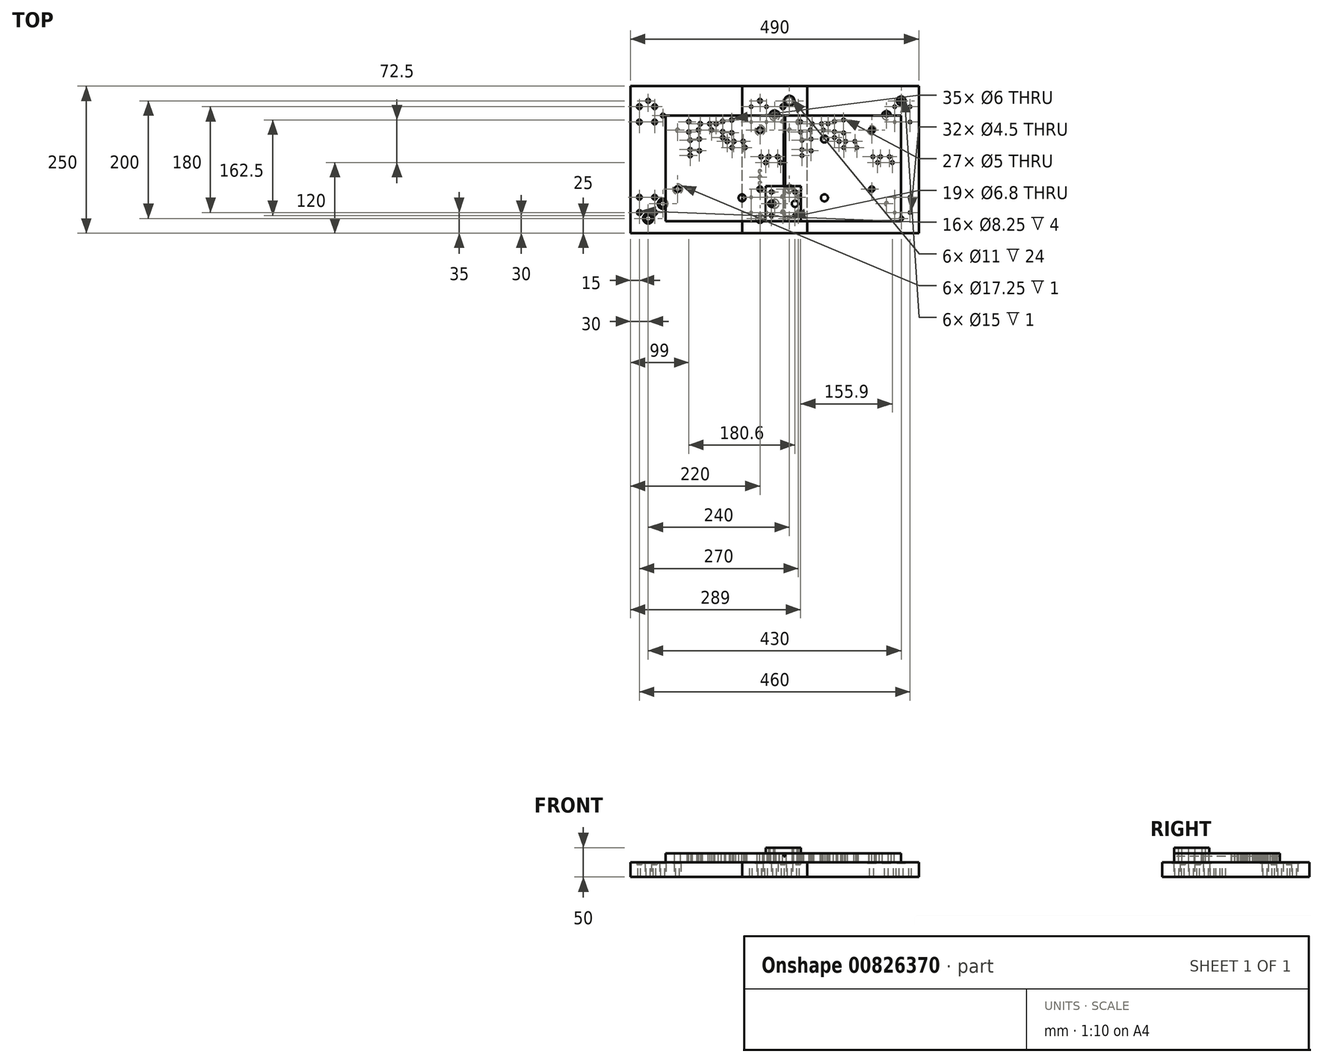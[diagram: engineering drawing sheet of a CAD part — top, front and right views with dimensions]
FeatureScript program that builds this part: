
annotation { "Feature Type Name" : "Feature", "Feature Type Description" : "" }
export const myFeature = defineFeature(function(context is Context, id is Id, definition is map)
    precondition{}
    {
        {
            var Q0;
            Q0=qCreatedBy(makeId("Top.planeOp"),FACE);
            var sketch = newSketch(context, id + "F0", { "sketchPlane" : qUnion([Q0])});
            skLineSegment(sketch, "E0.bottom", {"start": v(0, 0) * mm, "end": v(190, 0) * mm});
            skLineSegment(sketch, "E0.top", {"start": v(0, -180) * mm, "end": v(190, -180) * mm});
            skLineSegment(sketch, "E0.left", {"start": v(0, 0) * mm, "end": v(0, -180) * mm});
            skLineSegment(sketch, "E0.right", {"start": v(190, 0) * mm, "end": v(190, -180) * mm});
            skLineSegment(sketch, "E1", {"start": v(39.4, -10.5) * mm, "end": v(39.4, -28) * mm});
            skLineSegment(sketch, "E2", {"start": v(41.8, -42) * mm, "end": v(41.8, -58) * mm});
            skCircle(sketch, "E3", {"center": v(39.4, -10.5) * mm, "radius": 3 * mm});
            skCircle(sketch, "E4", {"center": v(39.4, -28) * mm, "radius": 3 * mm});
            skLineSegment(sketch, "E5", {"start": v(41.8, -58) * mm, "end": v(41.8, -68) * mm});
            skCircle(sketch, "E6", {"center": v(41.8, -42) * mm, "radius": 3 * mm});
            skCircle(sketch, "E7", {"center": v(41.8, -58) * mm, "radius": 3 * mm});
            skCircle(sketch, "E8", {"center": v(41.8, -68) * mm, "radius": 3 * mm});
            skLineSegment(sketch, "E9", {"start": v(59, -14) * mm, "end": v(75, -14) * mm});
            skLineSegment(sketch, "E10", {"start": v(75, -14) * mm, "end": v(86, -14) * mm});
            skLineSegment(sketch, "E11", {"start": v(56, -24.5) * mm, "end": v(78, -24.5) * mm});
            skCircle(sketch, "E12", {"center": v(59, -14) * mm, "radius": 3 * mm});
            skCircle(sketch, "E13", {"center": v(56, -24.5) * mm, "radius": 3 * mm});
            skCircle(sketch, "E14", {"center": v(78, -24.5) * mm, "radius": 3 * mm});
            skCircle(sketch, "E15", {"center": v(86, -14) * mm, "radius": 3 * mm});
            skCircle(sketch, "E16", {"center": v(75, -14) * mm, "radius": 3 * mm});
            skLineSegment(sketch, "E17", {"start": v(57.3, -40) * mm, "end": v(57.3, -60) * mm});
            skCircle(sketch, "E18", {"center": v(57.3, -40) * mm, "radius": 3 * mm});
            skCircle(sketch, "E19", {"center": v(57.3, -60) * mm, "radius": 3 * mm});
            skLineSegment(sketch, "E20", {"start": v(97, -10) * mm, "end": v(97, -27.5) * mm});
            skLineSegment(sketch, "E21", {"start": v(97, -27.5) * mm, "end": v(97, -37.5) * mm});
            skCircle(sketch, "E22", {"center": v(97, -10) * mm, "radius": 3 * mm});
            skCircle(sketch, "E23", {"center": v(97, -27.5) * mm, "radius": 3 * mm});
            skCircle(sketch, "E24", {"center": v(97, -37.5) * mm, "radius": 3 * mm});
            skLineSegment(sketch, "E25", {"start": v(104.9, -44) * mm, "end": v(112.9, -54.5) * mm});
            skLineSegment(sketch, "E26", {"start": v(112.9, -54.5) * mm, "end": v(134.9, -54.5) * mm});
            skCircle(sketch, "E27", {"center": v(104.9, -44) * mm, "radius": 3 * mm});
            skCircle(sketch, "E28", {"center": v(112.9, -54.5) * mm, "radius": 3 * mm});
            skCircle(sketch, "E29", {"center": v(134.9, -54.5) * mm, "radius": 3 * mm});
            skLineSegment(sketch, "E30", {"start": v(112.5, -7.5) * mm, "end": v(112.5, -29.5) * mm});
            skCircle(sketch, "E31", {"center": v(112.5, -7.5) * mm, "radius": 3 * mm});
            skCircle(sketch, "E32", {"center": v(112.5, -29.5) * mm, "radius": 3 * mm});
            skLineSegment(sketch, "E33", {"start": v(115.9, -44) * mm, "end": v(131.9, -44) * mm});
            skCircle(sketch, "E34", {"center": v(115.9, -44) * mm, "radius": 3 * mm});
            skCircle(sketch, "E35", {"center": v(131.9, -44) * mm, "radius": 3 * mm});
            skLineSegment(sketch, "E36.bottom", {"start": v(190, 0) * mm, "end": v(400, 0) * mm});
            skLineSegment(sketch, "E36.top", {"start": v(190, -180) * mm, "end": v(400, -180) * mm});
            skLineSegment(sketch, "E36.right", {"start": v(400, 0) * mm, "end": v(400, -180) * mm});
            skLineSegment(sketch, "E37", {"start": v(229.4, -10.5) * mm, "end": v(229.4, -28) * mm});
            skLineSegment(sketch, "E38", {"start": v(231.8, -42) * mm, "end": v(231.8, -58) * mm});
            skCircle(sketch, "E39", {"center": v(229.4, -10.5) * mm, "radius": 2.5 * mm});
            skCircle(sketch, "E40", {"center": v(229.4, -28) * mm, "radius": 2.5 * mm});
            skLineSegment(sketch, "E41", {"start": v(231.8, -58) * mm, "end": v(231.8, -68) * mm});
            skCircle(sketch, "E42", {"center": v(231.8, -42) * mm, "radius": 2.5 * mm});
            skCircle(sketch, "E43", {"center": v(231.8, -58) * mm, "radius": 2.5 * mm});
            skCircle(sketch, "E44", {"center": v(231.8, -68) * mm, "radius": 2.5 * mm});
            skLineSegment(sketch, "E45", {"start": v(249, -14) * mm, "end": v(265, -14) * mm});
            skLineSegment(sketch, "E46", {"start": v(265, -14) * mm, "end": v(276, -14) * mm});
            skLineSegment(sketch, "E47", {"start": v(246, -24.5) * mm, "end": v(268, -24.5) * mm});
            skCircle(sketch, "E48", {"center": v(249, -14) * mm, "radius": 2.5 * mm});
            skCircle(sketch, "E49", {"center": v(246, -24.5) * mm, "radius": 2.5 * mm});
            skCircle(sketch, "E50", {"center": v(268, -24.5) * mm, "radius": 2.5 * mm});
            skCircle(sketch, "E51", {"center": v(276, -14) * mm, "radius": 2.5 * mm});
            skCircle(sketch, "E52", {"center": v(265, -14) * mm, "radius": 2.5 * mm});
            skLineSegment(sketch, "E53", {"start": v(247.3, -40) * mm, "end": v(247.3, -60) * mm});
            skCircle(sketch, "E54", {"center": v(247.3, -40) * mm, "radius": 2.5 * mm});
            skCircle(sketch, "E55", {"center": v(247.3, -60) * mm, "radius": 2.5 * mm});
            skLineSegment(sketch, "E56", {"start": v(287, -10) * mm, "end": v(287, -27.5) * mm});
            skLineSegment(sketch, "E57", {"start": v(287, -27.5) * mm, "end": v(287, -37.5) * mm});
            skCircle(sketch, "E58", {"center": v(287, -10) * mm, "radius": 2.5 * mm});
            skCircle(sketch, "E59", {"center": v(287, -27.5) * mm, "radius": 2.5 * mm});
            skCircle(sketch, "E60", {"center": v(287, -37.5) * mm, "radius": 2.5 * mm});
            skLineSegment(sketch, "E61", {"start": v(294.9, -44) * mm, "end": v(302.9, -54.5) * mm});
            skLineSegment(sketch, "E62", {"start": v(302.9, -54.5) * mm, "end": v(324.9, -54.5) * mm});
            skCircle(sketch, "E63", {"center": v(294.9, -44) * mm, "radius": 2.5 * mm});
            skCircle(sketch, "E64", {"center": v(302.9, -54.5) * mm, "radius": 2.5 * mm});
            skCircle(sketch, "E65", {"center": v(324.9, -54.5) * mm, "radius": 2.5 * mm});
            skLineSegment(sketch, "E66", {"start": v(302.5, -7.5) * mm, "end": v(302.5, -29.5) * mm});
            skCircle(sketch, "E67", {"center": v(302.5, -7.5) * mm, "radius": 2.5 * mm});
            skCircle(sketch, "E68", {"center": v(302.5, -29.5) * mm, "radius": 2.5 * mm});
            skLineSegment(sketch, "E69", {"start": v(305.9, -44) * mm, "end": v(321.9, -44) * mm});
            skCircle(sketch, "E70", {"center": v(305.9, -44) * mm, "radius": 2.5 * mm});
            skCircle(sketch, "E71", {"center": v(321.9, -44) * mm, "radius": 2.5 * mm});
            skCircle(sketch, "E72", {"center": v(162.3, -70) * mm, "radius": 3 * mm});
            skCircle(sketch, "E73", {"center": v(175.3, -70) * mm, "radius": 3 * mm});
            skCircle(sketch, "E74", {"center": v(190.3, -70) * mm, "radius": 3 * mm});
            skCircle(sketch, "E75", {"center": v(170.3, -80) * mm, "radius": 3 * mm});
            skCircle(sketch, "E76", {"center": v(195.3, -80) * mm, "radius": 3 * mm});
            skLineSegment(sketch, "E77", {"start": v(162.3, -70) * mm, "end": v(175.3, -70) * mm});
            skLineSegment(sketch, "E78", {"start": v(175.3, -70) * mm, "end": v(190.3, -70) * mm});
            skLineSegment(sketch, "E79", {"start": v(170.3, -80) * mm, "end": v(195.3, -80) * mm});
            skCircle(sketch, "E80", {"center": v(352.3, -70) * mm, "radius": 2.5 * mm});
            skCircle(sketch, "E81", {"center": v(380.3, -70) * mm, "radius": 2.5 * mm});
            skCircle(sketch, "E82", {"center": v(365.3, -70) * mm, "radius": 2.5 * mm});
            skCircle(sketch, "E83", {"center": v(360.3, -80) * mm, "radius": 2.5 * mm});
            skCircle(sketch, "E84", {"center": v(385.3, -80) * mm, "radius": 2.5 * mm});
            skLineSegment(sketch, "E85", {"start": v(352.3, -70) * mm, "end": v(380.3, -70) * mm});
            skLineSegment(sketch, "E86", {"start": v(365.3, -70) * mm, "end": v(380.3, -70) * mm});
            skLineSegment(sketch, "E87", {"start": v(360.3, -80) * mm, "end": v(385.3, -80) * mm});
            skCircle(sketch, "E88", {"center": v(130, -140) * mm, "radius": 6 * mm});
            skCircle(sketch, "E89", {"center": v(270, -140) * mm, "radius": 6 * mm});
            skCircle(sketch, "E90", {"center": v(270, -40) * mm, "radius": 6 * mm});
            skLineSegment(sketch, "E91", {"start": v(200, -180) * mm, "end": v(200, 0) * mm});
            skSolve(sketch);
        }
        {
            var Q0;
            Q0 = qSketchRegion(id + "F0", true);
            extrude(context, id + "F1", {"entities" : qUnion([Q0]), "depth" : 15 * mm, "offsetDistance" : 25 * mm});
        }
        {
            var Q0;
            Q0=makeQuery(id+"F1.opExtrude","CAP_FACE",FACE,{"disambiguationData":[OSD([sQuery(id+"F0.wireOp",EDGE,"E0.bottom"),sQuery(id+"F0.wireOp",EDGE,"E0.top"),sQuery(id+"F0.wireOp",EDGE,"E0.left"),sQuery(id+"F0.wireOp",EDGE,"E3"),sQuery(id+"F0.wireOp",EDGE,"E4"),sQuery(id+"F0.wireOp",EDGE,"E6"),sQuery(id+"F0.wireOp",EDGE,"E7"),sQuery(id+"F0.wireOp",EDGE,"E8"),sQuery(id+"F0.wireOp",EDGE,"E12"),sQuery(id+"F0.wireOp",EDGE,"E13"),sQuery(id+"F0.wireOp",EDGE,"E14"),sQuery(id+"F0.wireOp",EDGE,"E15"),sQuery(id+"F0.wireOp",EDGE,"E16"),sQuery(id+"F0.wireOp",EDGE,"E18"),sQuery(id+"F0.wireOp",EDGE,"E19"),sQuery(id+"F0.wireOp",EDGE,"E22"),sQuery(id+"F0.wireOp",EDGE,"E23"),sQuery(id+"F0.wireOp",EDGE,"E24"),sQuery(id+"F0.wireOp",EDGE,"E27"),sQuery(id+"F0.wireOp",EDGE,"E28"),sQuery(id+"F0.wireOp",EDGE,"E29"),sQuery(id+"F0.wireOp",EDGE,"E31"),sQuery(id+"F0.wireOp",EDGE,"E32"),sQuery(id+"F0.wireOp",EDGE,"E34"),sQuery(id+"F0.wireOp",EDGE,"E35"),sQuery(id+"F0.wireOp",EDGE,"E36.bottom"),sQuery(id+"F0.wireOp",EDGE,"E36.top"),sQuery(id+"F0.wireOp",EDGE,"E36.right"),sQuery(id+"F0.wireOp",EDGE,"E39"),sQuery(id+"F0.wireOp",EDGE,"E40"),sQuery(id+"F0.wireOp",EDGE,"E42"),sQuery(id+"F0.wireOp",EDGE,"E43"),sQuery(id+"F0.wireOp",EDGE,"E44"),sQuery(id+"F0.wireOp",EDGE,"E48"),sQuery(id+"F0.wireOp",EDGE,"E49"),sQuery(id+"F0.wireOp",EDGE,"E50"),sQuery(id+"F0.wireOp",EDGE,"E51"),sQuery(id+"F0.wireOp",EDGE,"E52"),sQuery(id+"F0.wireOp",EDGE,"E54"),sQuery(id+"F0.wireOp",EDGE,"E55"),sQuery(id+"F0.wireOp",EDGE,"E58"),sQuery(id+"F0.wireOp",EDGE,"E59"),sQuery(id+"F0.wireOp",EDGE,"E60"),sQuery(id+"F0.wireOp",EDGE,"E63"),sQuery(id+"F0.wireOp",EDGE,"E64"),sQuery(id+"F0.wireOp",EDGE,"E65"),sQuery(id+"F0.wireOp",EDGE,"E67"),sQuery(id+"F0.wireOp",EDGE,"E68"),sQuery(id+"F0.wireOp",EDGE,"E70"),sQuery(id+"F0.wireOp",EDGE,"E71"),sQuery(id+"F0.wireOp",EDGE,"E72"),sQuery(id+"F0.wireOp",EDGE,"E73"),sQuery(id+"F0.wireOp",EDGE,"E74"),sQuery(id+"F0.wireOp",EDGE,"E75"),sQuery(id+"F0.wireOp",EDGE,"E76"),sQuery(id+"F0.wireOp",EDGE,"E80"),sQuery(id+"F0.wireOp",EDGE,"E81"),sQuery(id+"F0.wireOp",EDGE,"E82"),sQuery(id+"F0.wireOp",EDGE,"E83"),sQuery(id+"F0.wireOp",EDGE,"E84")])],"isStart":false});
            var sketch = newSketch(context, id + "F2", { "sketchPlane" : qUnion([Q0])});
            skLineSegment(sketch, "E92.bottom", {"start": v(170, -120) * mm, "end": v(230, -120) * mm});
            skLineSegment(sketch, "E92.top", {"start": v(170, -180) * mm, "end": v(230, -180) * mm});
            skLineSegment(sketch, "E92.left", {"start": v(170, -120) * mm, "end": v(170, -180) * mm});
            skLineSegment(sketch, "E92.right", {"start": v(230, -120) * mm, "end": v(230, -180) * mm});
            skCircle(sketch, "E93", {"center": v(180, -170) * mm, "radius": 2.5 * mm});
            skCircle(sketch, "E94", {"center": v(180, -150) * mm, "radius": 2.5 * mm});
            skCircle(sketch, "E95", {"center": v(180, -130) * mm, "radius": 2.5 * mm});
            skCircle(sketch, "E96", {"center": v(220, -130) * mm, "radius": 2.5 * mm});
            skCircle(sketch, "E97", {"center": v(220, -150) * mm, "radius": 2.5 * mm});
            skCircle(sketch, "E98", {"center": v(220, -170) * mm, "radius": 2.5 * mm});
            skPoint(sketch, "E99", {"position": v(200, -125.79) * mm});
            skPoint(sketch, "E100", {"position": v(170, -150) * mm});
            skPoint(sketch, "E101", {"position": v(200, -120) * mm});
            skSolve(sketch);
        }
        {
            var Q0;
            Q0 = qSketchRegion(id + "F2", true);
            extrude(context, id + "F3", {"entities" : qUnion([Q0]), "depth" : 10 * mm, "offsetDistance" : 25 * mm});
        }
        {
            var Q0;
            Q0=makeQuery(id+"F3.opExtrude","CAP_FACE",FACE,{"disambiguationData":[OSD([sQuery(id+"F2.wireOp",EDGE,"E92.bottom"),sQuery(id+"F2.wireOp",EDGE,"E92.top"),sQuery(id+"F2.wireOp",EDGE,"E92.left"),sQuery(id+"F2.wireOp",EDGE,"E92.right"),sQuery(id+"F2.wireOp",EDGE,"E93"),sQuery(id+"F2.wireOp",EDGE,"E94"),sQuery(id+"F2.wireOp",EDGE,"E95"),sQuery(id+"F2.wireOp",EDGE,"E96"),sQuery(id+"F2.wireOp",EDGE,"E97"),sQuery(id+"F2.wireOp",EDGE,"E98")])],"isStart":false});
            var sketch = newSketch(context, id + "F4", { "sketchPlane" : qUnion([Q0])});
            skPoint(sketch, "E102", {"position": v(180, -170) * mm});
            skPoint(sketch, "E103", {"position": v(180, -150) * mm});
            skPoint(sketch, "E104", {"position": v(180, -130) * mm});
            skPoint(sketch, "E105", {"position": v(220, -130) * mm});
            skPoint(sketch, "E106", {"position": v(220, -150) * mm});
            skPoint(sketch, "E107", {"position": v(220, -170) * mm});
            skSolve(sketch);
        }
        {
            var Q0;
            Q0=sQuery(id+"F4.wireOp",VERTEX,"E103");
            var Q1;
            Q1=sQuery(id+"F4.wireOp",VERTEX,"E106");
            var Q2;
            Q2=makeQuery(id+"F1.opExtrude","SWEPT_BODY",BODY,{"disambiguationData":[OSD([sQuery(id+"F0.wireOp",EDGE,"E0.bottom"),sQuery(id+"F0.wireOp",EDGE,"E0.top"),sQuery(id+"F0.wireOp",EDGE,"E0.left"),sQuery(id+"F0.wireOp",EDGE,"E3"),sQuery(id+"F0.wireOp",EDGE,"E4"),sQuery(id+"F0.wireOp",EDGE,"E6"),sQuery(id+"F0.wireOp",EDGE,"E7"),sQuery(id+"F0.wireOp",EDGE,"E8"),sQuery(id+"F0.wireOp",EDGE,"E12"),sQuery(id+"F0.wireOp",EDGE,"E13"),sQuery(id+"F0.wireOp",EDGE,"E14"),sQuery(id+"F0.wireOp",EDGE,"E15"),sQuery(id+"F0.wireOp",EDGE,"E16"),sQuery(id+"F0.wireOp",EDGE,"E18"),sQuery(id+"F0.wireOp",EDGE,"E19"),sQuery(id+"F0.wireOp",EDGE,"E22"),sQuery(id+"F0.wireOp",EDGE,"E23"),sQuery(id+"F0.wireOp",EDGE,"E24"),sQuery(id+"F0.wireOp",EDGE,"E27"),sQuery(id+"F0.wireOp",EDGE,"E28"),sQuery(id+"F0.wireOp",EDGE,"E29"),sQuery(id+"F0.wireOp",EDGE,"E31"),sQuery(id+"F0.wireOp",EDGE,"E32"),sQuery(id+"F0.wireOp",EDGE,"E34"),sQuery(id+"F0.wireOp",EDGE,"E35"),sQuery(id+"F0.wireOp",EDGE,"E36.bottom"),sQuery(id+"F0.wireOp",EDGE,"E36.top"),sQuery(id+"F0.wireOp",EDGE,"E36.right"),sQuery(id+"F0.wireOp",EDGE,"E39"),sQuery(id+"F0.wireOp",EDGE,"E40"),sQuery(id+"F0.wireOp",EDGE,"E42"),sQuery(id+"F0.wireOp",EDGE,"E43"),sQuery(id+"F0.wireOp",EDGE,"E44"),sQuery(id+"F0.wireOp",EDGE,"E48"),sQuery(id+"F0.wireOp",EDGE,"E49"),sQuery(id+"F0.wireOp",EDGE,"E50"),sQuery(id+"F0.wireOp",EDGE,"E51"),sQuery(id+"F0.wireOp",EDGE,"E52"),sQuery(id+"F0.wireOp",EDGE,"E54"),sQuery(id+"F0.wireOp",EDGE,"E55"),sQuery(id+"F0.wireOp",EDGE,"E58"),sQuery(id+"F0.wireOp",EDGE,"E59"),sQuery(id+"F0.wireOp",EDGE,"E60"),sQuery(id+"F0.wireOp",EDGE,"E63"),sQuery(id+"F0.wireOp",EDGE,"E64"),sQuery(id+"F0.wireOp",EDGE,"E65"),sQuery(id+"F0.wireOp",EDGE,"E67"),sQuery(id+"F0.wireOp",EDGE,"E68"),sQuery(id+"F0.wireOp",EDGE,"E70"),sQuery(id+"F0.wireOp",EDGE,"E71"),sQuery(id+"F0.wireOp",EDGE,"E72"),sQuery(id+"F0.wireOp",EDGE,"E73"),sQuery(id+"F0.wireOp",EDGE,"E74"),sQuery(id+"F0.wireOp",EDGE,"E75"),sQuery(id+"F0.wireOp",EDGE,"E76"),sQuery(id+"F0.wireOp",EDGE,"E80"),sQuery(id+"F0.wireOp",EDGE,"E81"),sQuery(id+"F0.wireOp",EDGE,"E82"),sQuery(id+"F0.wireOp",EDGE,"E83"),sQuery(id+"F0.wireOp",EDGE,"E84")])]});
            var Q3;
            Q3=makeQuery(id+"F3.opExtrude","SWEPT_BODY",BODY,{"disambiguationData":[OSD([sQuery(id+"F2.wireOp",EDGE,"E92.bottom"),sQuery(id+"F2.wireOp",EDGE,"E92.top"),sQuery(id+"F2.wireOp",EDGE,"E92.left"),sQuery(id+"F2.wireOp",EDGE,"E92.right"),sQuery(id+"F2.wireOp",EDGE,"E93"),sQuery(id+"F2.wireOp",EDGE,"E94"),sQuery(id+"F2.wireOp",EDGE,"E95"),sQuery(id+"F2.wireOp",EDGE,"E96"),sQuery(id+"F2.wireOp",EDGE,"E97"),sQuery(id+"F2.wireOp",EDGE,"E98")])]});
            hole(context, id + "F5", {"style" : HoleStyle.SIMPLE, "endStyle" : HoleEndStyle.BLIND, "holeDiameter" : 11 * mm, "majorDiameter" : 5 * mm, "holeDepth" : 50 * mm, "isTappedThrough" : true, "tappedDepth" : 12 * mm, "tapClearance" : 3, "locations" : qUnion([Q0, Q1]), "scope" : qUnion([Q2, Q3]), "startStyle" : HoleStartStyle.SKETCH});
        }
        {
            var Q0;
            Q0=sQuery(id+"F4.wireOp",VERTEX,"E104");
            var Q1;
            Q1=sQuery(id+"F4.wireOp",VERTEX,"E105");
            var Q2;
            Q2=sQuery(id+"F4.wireOp",VERTEX,"E107");
            var Q3;
            Q3=sQuery(id+"F4.wireOp",VERTEX,"E102");
            var Q4;
            Q4=makeQuery(id+"F1.opExtrude","SWEPT_BODY",BODY,{"disambiguationData":[OSD([sQuery(id+"F0.wireOp",EDGE,"E0.bottom"),sQuery(id+"F0.wireOp",EDGE,"E0.top"),sQuery(id+"F0.wireOp",EDGE,"E0.left"),sQuery(id+"F0.wireOp",EDGE,"E3"),sQuery(id+"F0.wireOp",EDGE,"E4"),sQuery(id+"F0.wireOp",EDGE,"E6"),sQuery(id+"F0.wireOp",EDGE,"E7"),sQuery(id+"F0.wireOp",EDGE,"E8"),sQuery(id+"F0.wireOp",EDGE,"E12"),sQuery(id+"F0.wireOp",EDGE,"E13"),sQuery(id+"F0.wireOp",EDGE,"E14"),sQuery(id+"F0.wireOp",EDGE,"E15"),sQuery(id+"F0.wireOp",EDGE,"E16"),sQuery(id+"F0.wireOp",EDGE,"E18"),sQuery(id+"F0.wireOp",EDGE,"E19"),sQuery(id+"F0.wireOp",EDGE,"E22"),sQuery(id+"F0.wireOp",EDGE,"E23"),sQuery(id+"F0.wireOp",EDGE,"E24"),sQuery(id+"F0.wireOp",EDGE,"E27"),sQuery(id+"F0.wireOp",EDGE,"E28"),sQuery(id+"F0.wireOp",EDGE,"E29"),sQuery(id+"F0.wireOp",EDGE,"E31"),sQuery(id+"F0.wireOp",EDGE,"E32"),sQuery(id+"F0.wireOp",EDGE,"E34"),sQuery(id+"F0.wireOp",EDGE,"E35"),sQuery(id+"F0.wireOp",EDGE,"E36.bottom"),sQuery(id+"F0.wireOp",EDGE,"E36.top"),sQuery(id+"F0.wireOp",EDGE,"E36.right"),sQuery(id+"F0.wireOp",EDGE,"E39"),sQuery(id+"F0.wireOp",EDGE,"E40"),sQuery(id+"F0.wireOp",EDGE,"E42"),sQuery(id+"F0.wireOp",EDGE,"E43"),sQuery(id+"F0.wireOp",EDGE,"E44"),sQuery(id+"F0.wireOp",EDGE,"E48"),sQuery(id+"F0.wireOp",EDGE,"E49"),sQuery(id+"F0.wireOp",EDGE,"E50"),sQuery(id+"F0.wireOp",EDGE,"E51"),sQuery(id+"F0.wireOp",EDGE,"E52"),sQuery(id+"F0.wireOp",EDGE,"E54"),sQuery(id+"F0.wireOp",EDGE,"E55"),sQuery(id+"F0.wireOp",EDGE,"E58"),sQuery(id+"F0.wireOp",EDGE,"E59"),sQuery(id+"F0.wireOp",EDGE,"E60"),sQuery(id+"F0.wireOp",EDGE,"E63"),sQuery(id+"F0.wireOp",EDGE,"E64"),sQuery(id+"F0.wireOp",EDGE,"E65"),sQuery(id+"F0.wireOp",EDGE,"E67"),sQuery(id+"F0.wireOp",EDGE,"E68"),sQuery(id+"F0.wireOp",EDGE,"E70"),sQuery(id+"F0.wireOp",EDGE,"E71"),sQuery(id+"F0.wireOp",EDGE,"E72"),sQuery(id+"F0.wireOp",EDGE,"E73"),sQuery(id+"F0.wireOp",EDGE,"E74"),sQuery(id+"F0.wireOp",EDGE,"E75"),sQuery(id+"F0.wireOp",EDGE,"E76"),sQuery(id+"F0.wireOp",EDGE,"E80"),sQuery(id+"F0.wireOp",EDGE,"E81"),sQuery(id+"F0.wireOp",EDGE,"E82"),sQuery(id+"F0.wireOp",EDGE,"E83"),sQuery(id+"F0.wireOp",EDGE,"E84"),sQuery(id+"F0.wireOp",EDGE,"E88"),sQuery(id+"F0.wireOp",EDGE,"E89"),sQuery(id+"F0.wireOp",EDGE,"E90")])]});
            var Q5;
            Q5=makeQuery(id+"F3.opExtrude","SWEPT_BODY",BODY,{"disambiguationData":[OSD([sQuery(id+"F2.wireOp",EDGE,"E92.bottom"),sQuery(id+"F2.wireOp",EDGE,"E92.top"),sQuery(id+"F2.wireOp",EDGE,"E92.left"),sQuery(id+"F2.wireOp",EDGE,"E92.right"),sQuery(id+"F2.wireOp",EDGE,"E93"),sQuery(id+"F2.wireOp",EDGE,"E94"),sQuery(id+"F2.wireOp",EDGE,"E95"),sQuery(id+"F2.wireOp",EDGE,"E96"),sQuery(id+"F2.wireOp",EDGE,"E97"),sQuery(id+"F2.wireOp",EDGE,"E98")])]});
            hole(context, id + "F6", {"style" : HoleStyle.SIMPLE, "endStyle" : HoleEndStyle.BLIND, "holeDiameter" : 6 * mm, "majorDiameter" : 5 * mm, "holeDepth" : 50 * mm, "isTappedThrough" : true, "tappedDepth" : 12 * mm, "tapClearance" : 3, "locations" : qUnion([Q0, Q1, Q2, Q3]), "scope" : qUnion([Q4, Q5]), "startStyle" : HoleStartStyle.SKETCH});
        }
        {
            var Q0;
            {var subQ7=sQuery(id+"F0.wireOp",EDGE,"E0.bottom");Q0=makeQuery(id+"F0.imprint","IMPRINT",FACE,{"disambiguationData":[TD([[makeQuery(id+"F0.imprint","IMPRINT",EDGE,{"derivedFrom":subQ7}),-1.0]])]});}
            var sketch = newSketch(context, id + "F7", { "sketchPlane" : qUnion([Q0])});
            skLineSegment(sketch, "E108.bottom", {"start": v(-59.6, -200) * mm, "end": v(240.4, -200) * mm});
            skLineSegment(sketch, "E108.top", {"start": v(-59.6, 50) * mm, "end": v(240.4, 50) * mm});
            skLineSegment(sketch, "E108.left", {"start": v(-59.6, -200) * mm, "end": v(-59.6, 50) * mm});
            skLineSegment(sketch, "E108.right", {"start": v(240.4, -200) * mm, "end": v(240.4, 50) * mm});
            skCircle(sketch, "E109", {"center": v(-44.6, -165) * mm, "radius": 2.25 * mm});
            skCircle(sketch, "E110", {"center": v(-18.6, -165) * mm, "radius": 2.25 * mm});
            skCircle(sketch, "E111", {"center": v(-18.6, -139) * mm, "radius": 2.25 * mm});
            skCircle(sketch, "E112", {"center": v(-44.6, -139) * mm, "radius": 2.25 * mm});
            skCircle(sketch, "E113", {"center": v(199.4, -165) * mm, "radius": 2.25 * mm});
            skCircle(sketch, "E114", {"center": v(225.4, -165) * mm, "radius": 2.25 * mm});
            skCircle(sketch, "E115", {"center": v(225.4, -139) * mm, "radius": 2.25 * mm});
            skCircle(sketch, "E116", {"center": v(199.4, -139) * mm, "radius": 2.25 * mm});
            skCircle(sketch, "E117", {"center": v(-44.6, -11) * mm, "radius": 2.25 * mm});
            skCircle(sketch, "E118", {"center": v(-18.6, -11) * mm, "radius": 2.25 * mm});
            skCircle(sketch, "E119", {"center": v(-18.6, 15) * mm, "radius": 2.25 * mm});
            skCircle(sketch, "E120", {"center": v(-44.6, 15) * mm, "radius": 2.25 * mm});
            skCircle(sketch, "E121", {"center": v(199.4, -11) * mm, "radius": 2.25 * mm});
            skCircle(sketch, "E122", {"center": v(225.4, -11) * mm, "radius": 2.25 * mm});
            skCircle(sketch, "E123", {"center": v(225.4, 15) * mm, "radius": 2.25 * mm});
            skCircle(sketch, "E124", {"center": v(199.4, 15) * mm, "radius": 2.25 * mm});
            skCircle(sketch, "E125", {"center": v(20.4, -125) * mm, "radius": 3.4 * mm});
            skCircle(sketch, "E126", {"center": v(-4.6, -150) * mm, "radius": 3.4 * mm});
            skCircle(sketch, "E127", {"center": v(-29.6, -175) * mm, "radius": 3.4 * mm});
            skCircle(sketch, "E128", {"center": v(-29.6, 25) * mm, "radius": 3.4 * mm});
            skCircle(sketch, "E129", {"center": v(210.4, 25) * mm, "radius": 3.4 * mm});
            skCircle(sketch, "E130", {"center": v(185.4, 0) * mm, "radius": 3.4 * mm});
            skCircle(sketch, "E131", {"center": v(160.4, -25) * mm, "radius": 3.4 * mm});
            skCircle(sketch, "E132", {"center": v(-4.6, 0) * mm, "radius": 3.4 * mm});
            skCircle(sketch, "E133", {"center": v(20.4, -25) * mm, "radius": 3.4 * mm});
            skCircle(sketch, "E134", {"center": v(160.4, -125) * mm, "radius": 3.4 * mm});
            skCircle(sketch, "E135", {"center": v(185.4, -150) * mm, "radius": 3.4 * mm});
            skCircle(sketch, "E136", {"center": v(210.4, -175) * mm, "radius": 3.4 * mm});
            skLineSegment(sketch, "E137", {"start": v(90.4, -200) * mm, "end": v(90.4, 50) * mm});
            skLineSegment(sketch, "E138", {"start": v(-59.6, -75) * mm, "end": v(240.4, -75) * mm});
            skLineSegment(sketch, "E139", {"start": v(27.14, 50) * mm, "end": v(27.14, 0) * mm});
            skSolve(sketch);
        }
        {
            var Q0;
            Q0 = qSketchRegion(id + "F7", true);
            extrude(context, id + "F8", {"entities" : qUnion([Q0]), "oppositeDirection" : true, "depth" : 25 * mm, "offsetDistance" : 25 * mm});
        }
        {
            var Q0;
            Q0=makeQuery(id+"F8.opExtrude","CAP_FACE",FACE,{"disambiguationData":[OSD([sQuery(id+"F7.wireOp",EDGE,"E108.bottom"),sQuery(id+"F7.wireOp",EDGE,"E108.top"),sQuery(id+"F7.wireOp",EDGE,"E108.left"),sQuery(id+"F7.wireOp",EDGE,"E108.right"),sQuery(id+"F7.wireOp",EDGE,"E109"),sQuery(id+"F7.wireOp",EDGE,"E110"),sQuery(id+"F7.wireOp",EDGE,"E111"),sQuery(id+"F7.wireOp",EDGE,"E112"),sQuery(id+"F7.wireOp",EDGE,"E113"),sQuery(id+"F7.wireOp",EDGE,"E114"),sQuery(id+"F7.wireOp",EDGE,"E115"),sQuery(id+"F7.wireOp",EDGE,"E116"),sQuery(id+"F7.wireOp",EDGE,"E117"),sQuery(id+"F7.wireOp",EDGE,"E118"),sQuery(id+"F7.wireOp",EDGE,"E119"),sQuery(id+"F7.wireOp",EDGE,"E120"),sQuery(id+"F7.wireOp",EDGE,"E121"),sQuery(id+"F7.wireOp",EDGE,"E122"),sQuery(id+"F7.wireOp",EDGE,"E123"),sQuery(id+"F7.wireOp",EDGE,"E124"),sQuery(id+"F7.wireOp",EDGE,"E125"),sQuery(id+"F7.wireOp",EDGE,"E126"),sQuery(id+"F7.wireOp",EDGE,"E127"),sQuery(id+"F7.wireOp",EDGE,"E128"),sQuery(id+"F7.wireOp",EDGE,"E129"),sQuery(id+"F7.wireOp",EDGE,"E130"),sQuery(id+"F7.wireOp",EDGE,"E131"),sQuery(id+"F7.wireOp",EDGE,"E132"),sQuery(id+"F7.wireOp",EDGE,"E133"),sQuery(id+"F7.wireOp",EDGE,"E134"),sQuery(id+"F7.wireOp",EDGE,"E135"),sQuery(id+"F7.wireOp",EDGE,"E136")])],"isStart":true});
            var sketch = newSketch(context, id + "F9", { "sketchPlane" : qUnion([Q0])});
            skCircle(sketch, "E140", {"center": v(160.4, -115) * mm, "radius": 3 * mm});
            skCircle(sketch, "E141", {"center": v(160.4, -105) * mm, "radius": 3.4 * mm});
            skCircle(sketch, "E142", {"center": v(160.4, -95) * mm, "radius": 3 * mm});
            skLineSegment(sketch, "E143", {"start": v(160.4, -25) * mm, "end": v(160.4, -125) * mm});
            skSolve(sketch);
        }
        {
            var Q0;
            Q0 = qSketchRegion(id + "F9", true);
            extrude(context, id + "F10", {"entities" : qUnion([Q0]), "operationType" : NewBodyOperationType.REMOVE, "oppositeDirection" : true, "depth" : 25 * mm, "offsetDistance" : 25 * mm});
        }
        {
            var Q0;
            Q0=sQuery(id+"F7.wireOp",VERTEX,"E111.center");
            var Q1;
            Q1=sQuery(id+"F7.wireOp",VERTEX,"E112.center");
            var Q2;
            Q2=sQuery(id+"F7.wireOp",VERTEX,"E109.center");
            var Q3;
            Q3=sQuery(id+"F7.wireOp",VERTEX,"E110.center");
            var Q4;
            Q4=sQuery(id+"F7.wireOp",VERTEX,"E113.center");
            var Q5;
            Q5=sQuery(id+"F7.wireOp",VERTEX,"E116.center");
            var Q6;
            Q6=sQuery(id+"F7.wireOp",VERTEX,"E115.center");
            var Q7;
            Q7=sQuery(id+"F7.wireOp",VERTEX,"E114.center");
            var Q8;
            Q8=sQuery(id+"F7.wireOp",VERTEX,"E121.center");
            var Q9;
            Q9=sQuery(id+"F7.wireOp",VERTEX,"E124.center");
            var Q10;
            Q10=sQuery(id+"F7.wireOp",VERTEX,"E123.center");
            var Q11;
            Q11=sQuery(id+"F7.wireOp",VERTEX,"E122.center");
            var Q12;
            Q12=sQuery(id+"F7.wireOp",VERTEX,"E118.center");
            var Q13;
            Q13=sQuery(id+"F7.wireOp",VERTEX,"E119.center");
            var Q14;
            Q14=sQuery(id+"F7.wireOp",VERTEX,"E120.center");
            var Q15;
            Q15=sQuery(id+"F7.wireOp",VERTEX,"E117.center");
            var Q16;
            Q16=makeQuery(id+"F8.opExtrude","SWEPT_BODY",BODY,{"disambiguationData":[OSD([sQuery(id+"F7.wireOp",EDGE,"E108.bottom"),sQuery(id+"F7.wireOp",EDGE,"E108.top"),sQuery(id+"F7.wireOp",EDGE,"E108.left"),sQuery(id+"F7.wireOp",EDGE,"E108.right"),sQuery(id+"F7.wireOp",EDGE,"E109"),sQuery(id+"F7.wireOp",EDGE,"E110"),sQuery(id+"F7.wireOp",EDGE,"E111"),sQuery(id+"F7.wireOp",EDGE,"E112"),sQuery(id+"F7.wireOp",EDGE,"E113"),sQuery(id+"F7.wireOp",EDGE,"E114"),sQuery(id+"F7.wireOp",EDGE,"E115"),sQuery(id+"F7.wireOp",EDGE,"E116"),sQuery(id+"F7.wireOp",EDGE,"E117"),sQuery(id+"F7.wireOp",EDGE,"E118"),sQuery(id+"F7.wireOp",EDGE,"E119"),sQuery(id+"F7.wireOp",EDGE,"E120"),sQuery(id+"F7.wireOp",EDGE,"E121"),sQuery(id+"F7.wireOp",EDGE,"E122"),sQuery(id+"F7.wireOp",EDGE,"E123"),sQuery(id+"F7.wireOp",EDGE,"E124"),sQuery(id+"F7.wireOp",EDGE,"E125"),sQuery(id+"F7.wireOp",EDGE,"E126"),sQuery(id+"F7.wireOp",EDGE,"E127"),sQuery(id+"F7.wireOp",EDGE,"E128"),sQuery(id+"F7.wireOp",EDGE,"E129"),sQuery(id+"F7.wireOp",EDGE,"E130"),sQuery(id+"F7.wireOp",EDGE,"E131"),sQuery(id+"F7.wireOp",EDGE,"E132"),sQuery(id+"F7.wireOp",EDGE,"E133"),sQuery(id+"F7.wireOp",EDGE,"E134"),sQuery(id+"F7.wireOp",EDGE,"E135"),sQuery(id+"F7.wireOp",EDGE,"E136")])]});
            hole(context, id + "F11", {"style" : HoleStyle.C_BORE, "endStyle" : HoleEndStyle.BLIND, "standardTappedOrClearance" : lookupTablePath({ "fit" : "Normal", "standard" : "ISO", "size" : "M4", "type" : "Clearance" }), "standardBlindInLast" : lookupTablePath({ "fit" : "Normal", "standard" : "ISO", "size" : "M4", "type" : "Clearance" }), "holeDiameter" : 4.5 * mm, "cBoreDiameter" : 8.25 * mm, "cBoreDepth" : 4 * mm, "majorDiameter" : 5 * mm, "holeDepth" : 50 * mm, "isTappedThrough" : true, "tappedDepth" : 12 * mm, "tapClearance" : 3, "locations" : qUnion([Q0, Q1, Q2, Q3, Q4, Q5, Q6, Q7, Q8, Q9, Q10, Q11, Q12, Q13, Q14, Q15]), "scope" : qUnion([Q16]), "startStyle" : HoleStartStyle.SKETCH});
        }
        {
            var Q0;
            Q0=sQuery(id+"F7.wireOp",VERTEX,"E129.center");
            var Q1;
            Q1=sQuery(id+"F7.wireOp",VERTEX,"E130.center");
            var Q2;
            Q2=sQuery(id+"F7.wireOp",VERTEX,"E131.center");
            var Q3;
            Q3=sQuery(id+"F7.wireOp",VERTEX,"E125.center");
            var Q4;
            Q4=sQuery(id+"F7.wireOp",VERTEX,"E126.center");
            var Q5;
            Q5=sQuery(id+"F7.wireOp",VERTEX,"E127.center");
            var Q6;
            Q6=makeQuery(id+"F8.opExtrude","SWEPT_BODY",BODY,{"disambiguationData":[OSD([sQuery(id+"F7.wireOp",EDGE,"E108.bottom"),sQuery(id+"F7.wireOp",EDGE,"E108.top"),sQuery(id+"F7.wireOp",EDGE,"E108.left"),sQuery(id+"F7.wireOp",EDGE,"E108.right"),sQuery(id+"F7.wireOp",EDGE,"E109"),sQuery(id+"F7.wireOp",EDGE,"E110"),sQuery(id+"F7.wireOp",EDGE,"E111"),sQuery(id+"F7.wireOp",EDGE,"E112"),sQuery(id+"F7.wireOp",EDGE,"E113"),sQuery(id+"F7.wireOp",EDGE,"E114"),sQuery(id+"F7.wireOp",EDGE,"E115"),sQuery(id+"F7.wireOp",EDGE,"E116"),sQuery(id+"F7.wireOp",EDGE,"E117"),sQuery(id+"F7.wireOp",EDGE,"E118"),sQuery(id+"F7.wireOp",EDGE,"E119"),sQuery(id+"F7.wireOp",EDGE,"E120"),sQuery(id+"F7.wireOp",EDGE,"E121"),sQuery(id+"F7.wireOp",EDGE,"E122"),sQuery(id+"F7.wireOp",EDGE,"E123"),sQuery(id+"F7.wireOp",EDGE,"E124"),sQuery(id+"F7.wireOp",EDGE,"E125"),sQuery(id+"F7.wireOp",EDGE,"E126"),sQuery(id+"F7.wireOp",EDGE,"E127"),sQuery(id+"F7.wireOp",EDGE,"E128"),sQuery(id+"F7.wireOp",EDGE,"E129"),sQuery(id+"F7.wireOp",EDGE,"E130"),sQuery(id+"F7.wireOp",EDGE,"E131"),sQuery(id+"F7.wireOp",EDGE,"E132"),sQuery(id+"F7.wireOp",EDGE,"E133"),sQuery(id+"F7.wireOp",EDGE,"E134"),sQuery(id+"F7.wireOp",EDGE,"E135"),sQuery(id+"F7.wireOp",EDGE,"E136")])]});
            hole(context, id + "F12", {"style" : HoleStyle.C_BORE, "endStyle" : HoleEndStyle.BLIND, "holeDiameter" : 11 * mm, "cBoreDiameter" : 17.25 * mm, "cBoreDepth" : 1 * mm, "majorDiameter" : 5 * mm, "holeDepth" : 50 * mm, "isTappedThrough" : true, "tappedDepth" : 12 * mm, "tapClearance" : 3, "locations" : qUnion([Q0, Q1, Q2, Q3, Q4, Q5]), "scope" : qUnion([Q6]), "startStyle" : HoleStartStyle.SKETCH});
        }
        {
            var Q0;
            Q0=sQuery(id+"F7.wireOp",VERTEX,"E134.center");
            var Q1;
            Q1=makeQuery(id+"F1.opExtrude","SWEPT_BODY",BODY,{"disambiguationData":[OSD([sQuery(id+"F0.wireOp",EDGE,"E0.bottom"),sQuery(id+"F0.wireOp",EDGE,"E0.top"),sQuery(id+"F0.wireOp",EDGE,"E0.left"),sQuery(id+"F0.wireOp",EDGE,"E3"),sQuery(id+"F0.wireOp",EDGE,"E4"),sQuery(id+"F0.wireOp",EDGE,"E6"),sQuery(id+"F0.wireOp",EDGE,"E7"),sQuery(id+"F0.wireOp",EDGE,"E8"),sQuery(id+"F0.wireOp",EDGE,"E12"),sQuery(id+"F0.wireOp",EDGE,"E13"),sQuery(id+"F0.wireOp",EDGE,"E14"),sQuery(id+"F0.wireOp",EDGE,"E15"),sQuery(id+"F0.wireOp",EDGE,"E16"),sQuery(id+"F0.wireOp",EDGE,"E18"),sQuery(id+"F0.wireOp",EDGE,"E19"),sQuery(id+"F0.wireOp",EDGE,"E22"),sQuery(id+"F0.wireOp",EDGE,"E23"),sQuery(id+"F0.wireOp",EDGE,"E24"),sQuery(id+"F0.wireOp",EDGE,"E27"),sQuery(id+"F0.wireOp",EDGE,"E28"),sQuery(id+"F0.wireOp",EDGE,"E29"),sQuery(id+"F0.wireOp",EDGE,"E31"),sQuery(id+"F0.wireOp",EDGE,"E32"),sQuery(id+"F0.wireOp",EDGE,"E34"),sQuery(id+"F0.wireOp",EDGE,"E35"),sQuery(id+"F0.wireOp",EDGE,"E36.bottom"),sQuery(id+"F0.wireOp",EDGE,"E36.top"),sQuery(id+"F0.wireOp",EDGE,"E36.right"),sQuery(id+"F0.wireOp",EDGE,"E39"),sQuery(id+"F0.wireOp",EDGE,"E40"),sQuery(id+"F0.wireOp",EDGE,"E42"),sQuery(id+"F0.wireOp",EDGE,"E43"),sQuery(id+"F0.wireOp",EDGE,"E44"),sQuery(id+"F0.wireOp",EDGE,"E48"),sQuery(id+"F0.wireOp",EDGE,"E49"),sQuery(id+"F0.wireOp",EDGE,"E50"),sQuery(id+"F0.wireOp",EDGE,"E51"),sQuery(id+"F0.wireOp",EDGE,"E52"),sQuery(id+"F0.wireOp",EDGE,"E54"),sQuery(id+"F0.wireOp",EDGE,"E55"),sQuery(id+"F0.wireOp",EDGE,"E58"),sQuery(id+"F0.wireOp",EDGE,"E59"),sQuery(id+"F0.wireOp",EDGE,"E60"),sQuery(id+"F0.wireOp",EDGE,"E63"),sQuery(id+"F0.wireOp",EDGE,"E64"),sQuery(id+"F0.wireOp",EDGE,"E65"),sQuery(id+"F0.wireOp",EDGE,"E67"),sQuery(id+"F0.wireOp",EDGE,"E68"),sQuery(id+"F0.wireOp",EDGE,"E70"),sQuery(id+"F0.wireOp",EDGE,"E71"),sQuery(id+"F0.wireOp",EDGE,"E72"),sQuery(id+"F0.wireOp",EDGE,"E73"),sQuery(id+"F0.wireOp",EDGE,"E74"),sQuery(id+"F0.wireOp",EDGE,"E75"),sQuery(id+"F0.wireOp",EDGE,"E76"),sQuery(id+"F0.wireOp",EDGE,"E80"),sQuery(id+"F0.wireOp",EDGE,"E81"),sQuery(id+"F0.wireOp",EDGE,"E82"),sQuery(id+"F0.wireOp",EDGE,"E83"),sQuery(id+"F0.wireOp",EDGE,"E84"),sQuery(id+"F0.wireOp",EDGE,"E88"),sQuery(id+"F0.wireOp",EDGE,"E89"),sQuery(id+"F0.wireOp",EDGE,"E90")])]});
            hole(context, id + "F13", {"style" : HoleStyle.SIMPLE, "endStyle" : HoleEndStyle.BLIND, "oppositeDirection" : true, "holeDiameter" : 9 * mm, "majorDiameter" : 5 * mm, "holeDepth" : 50 * mm, "isTappedThrough" : true, "tappedDepth" : 12 * mm, "tapClearance" : 3, "locations" : qUnion([Q0]), "scope" : qUnion([Q1]), "startStyle" : HoleStartStyle.SKETCH});
        }
        {
            var Q0;
            Q0=sQuery(id+"F7.wireOp",VERTEX,"E125.center");
            var Q1;
            Q1=sQuery(id+"F7.wireOp",VERTEX,"E131.center");
            var Q2;
            Q2=makeQuery(id+"F1.opExtrude","SWEPT_BODY",BODY,{"disambiguationData":[OSD([sQuery(id+"F0.wireOp",EDGE,"E0.bottom"),sQuery(id+"F0.wireOp",EDGE,"E0.top"),sQuery(id+"F0.wireOp",EDGE,"E0.left"),sQuery(id+"F0.wireOp",EDGE,"E3"),sQuery(id+"F0.wireOp",EDGE,"E4"),sQuery(id+"F0.wireOp",EDGE,"E6"),sQuery(id+"F0.wireOp",EDGE,"E7"),sQuery(id+"F0.wireOp",EDGE,"E8"),sQuery(id+"F0.wireOp",EDGE,"E12"),sQuery(id+"F0.wireOp",EDGE,"E13"),sQuery(id+"F0.wireOp",EDGE,"E14"),sQuery(id+"F0.wireOp",EDGE,"E15"),sQuery(id+"F0.wireOp",EDGE,"E16"),sQuery(id+"F0.wireOp",EDGE,"E18"),sQuery(id+"F0.wireOp",EDGE,"E19"),sQuery(id+"F0.wireOp",EDGE,"E22"),sQuery(id+"F0.wireOp",EDGE,"E23"),sQuery(id+"F0.wireOp",EDGE,"E24"),sQuery(id+"F0.wireOp",EDGE,"E27"),sQuery(id+"F0.wireOp",EDGE,"E28"),sQuery(id+"F0.wireOp",EDGE,"E29"),sQuery(id+"F0.wireOp",EDGE,"E31"),sQuery(id+"F0.wireOp",EDGE,"E32"),sQuery(id+"F0.wireOp",EDGE,"E34"),sQuery(id+"F0.wireOp",EDGE,"E35"),sQuery(id+"F0.wireOp",EDGE,"E36.bottom"),sQuery(id+"F0.wireOp",EDGE,"E36.top"),sQuery(id+"F0.wireOp",EDGE,"E36.right"),sQuery(id+"F0.wireOp",EDGE,"E39"),sQuery(id+"F0.wireOp",EDGE,"E40"),sQuery(id+"F0.wireOp",EDGE,"E42"),sQuery(id+"F0.wireOp",EDGE,"E43"),sQuery(id+"F0.wireOp",EDGE,"E44"),sQuery(id+"F0.wireOp",EDGE,"E48"),sQuery(id+"F0.wireOp",EDGE,"E49"),sQuery(id+"F0.wireOp",EDGE,"E50"),sQuery(id+"F0.wireOp",EDGE,"E51"),sQuery(id+"F0.wireOp",EDGE,"E52"),sQuery(id+"F0.wireOp",EDGE,"E54"),sQuery(id+"F0.wireOp",EDGE,"E55"),sQuery(id+"F0.wireOp",EDGE,"E58"),sQuery(id+"F0.wireOp",EDGE,"E59"),sQuery(id+"F0.wireOp",EDGE,"E60"),sQuery(id+"F0.wireOp",EDGE,"E63"),sQuery(id+"F0.wireOp",EDGE,"E64"),sQuery(id+"F0.wireOp",EDGE,"E65"),sQuery(id+"F0.wireOp",EDGE,"E67"),sQuery(id+"F0.wireOp",EDGE,"E68"),sQuery(id+"F0.wireOp",EDGE,"E70"),sQuery(id+"F0.wireOp",EDGE,"E71"),sQuery(id+"F0.wireOp",EDGE,"E72"),sQuery(id+"F0.wireOp",EDGE,"E73"),sQuery(id+"F0.wireOp",EDGE,"E74"),sQuery(id+"F0.wireOp",EDGE,"E75"),sQuery(id+"F0.wireOp",EDGE,"E76"),sQuery(id+"F0.wireOp",EDGE,"E80"),sQuery(id+"F0.wireOp",EDGE,"E81"),sQuery(id+"F0.wireOp",EDGE,"E82"),sQuery(id+"F0.wireOp",EDGE,"E83"),sQuery(id+"F0.wireOp",EDGE,"E84"),sQuery(id+"F0.wireOp",EDGE,"E88"),sQuery(id+"F0.wireOp",EDGE,"E89"),sQuery(id+"F0.wireOp",EDGE,"E90")])]});
            hole(context, id + "F14", {"style" : HoleStyle.SIMPLE, "endStyle" : HoleEndStyle.BLIND, "oppositeDirection" : true, "holeDiameter" : 10 * mm, "majorDiameter" : 5 * mm, "holeDepth" : 50 * mm, "isTappedThrough" : true, "tappedDepth" : 12 * mm, "tapClearance" : 3, "locations" : qUnion([Q0, Q1]), "scope" : qUnion([Q2]), "startStyle" : HoleStartStyle.SKETCH});
        }
        {
            var Q0;
            {var subQ6=sQuery(id+"F0.wireOp",EDGE,"E36.right");Q0=makeQuery(id+"F0.imprint","IMPRINT",FACE,{"disambiguationData":[TD([[makeQuery(id+"F0.imprint","IMPRINT",EDGE,{"derivedFrom":subQ6}),-1.0]])]});}
            var sketch = newSketch(context, id + "F15", { "sketchPlane" : qUnion([Q0])});
            skLineSegment(sketch, "E144.bottom", {"start": v(130.4, -200) * mm, "end": v(430.4, -200) * mm});
            skLineSegment(sketch, "E144.top", {"start": v(130.4, 50) * mm, "end": v(430.4, 50) * mm});
            skLineSegment(sketch, "E144.left", {"start": v(130.4, -200) * mm, "end": v(130.4, 50) * mm});
            skLineSegment(sketch, "E144.right", {"start": v(430.4, -200) * mm, "end": v(430.4, 50) * mm});
            skCircle(sketch, "E145", {"center": v(145.4, -165) * mm, "radius": 2.25 * mm});
            skCircle(sketch, "E146", {"center": v(171.4, -165) * mm, "radius": 2.25 * mm});
            skCircle(sketch, "E147", {"center": v(171.4, -139) * mm, "radius": 2.25 * mm});
            skCircle(sketch, "E148", {"center": v(145.4, -139) * mm, "radius": 2.25 * mm});
            skCircle(sketch, "E149", {"center": v(389.4, -165) * mm, "radius": 2.25 * mm});
            skCircle(sketch, "E150", {"center": v(415.4, -165) * mm, "radius": 2.25 * mm});
            skCircle(sketch, "E151", {"center": v(415.4, -139) * mm, "radius": 2.25 * mm});
            skCircle(sketch, "E152", {"center": v(389.4, -139) * mm, "radius": 2.25 * mm});
            skCircle(sketch, "E153", {"center": v(145.4, -11) * mm, "radius": 2.25 * mm});
            skCircle(sketch, "E154", {"center": v(171.4, -11) * mm, "radius": 2.25 * mm});
            skCircle(sketch, "E155", {"center": v(171.4, 15) * mm, "radius": 2.25 * mm});
            skCircle(sketch, "E156", {"center": v(145.4, 15) * mm, "radius": 2.25 * mm});
            skCircle(sketch, "E157", {"center": v(389.4, -11) * mm, "radius": 2.25 * mm});
            skCircle(sketch, "E158", {"center": v(415.4, -11) * mm, "radius": 2.25 * mm});
            skCircle(sketch, "E159", {"center": v(415.4, 15) * mm, "radius": 2.25 * mm});
            skCircle(sketch, "E160", {"center": v(389.4, 15) * mm, "radius": 2.25 * mm});
            skCircle(sketch, "E161", {"center": v(210.4, -125) * mm, "radius": 3.4 * mm});
            skCircle(sketch, "E162", {"center": v(185.4, -150) * mm, "radius": 3.4 * mm});
            skCircle(sketch, "E163", {"center": v(160.4, -175) * mm, "radius": 3.4 * mm});
            skCircle(sketch, "E164", {"center": v(160.4, 25) * mm, "radius": 3.4 * mm});
            skCircle(sketch, "E165", {"center": v(400.4, 25) * mm, "radius": 3.4 * mm});
            skCircle(sketch, "E166", {"center": v(375.4, 0) * mm, "radius": 3.4 * mm});
            skCircle(sketch, "E167", {"center": v(350.4, -25) * mm, "radius": 3.4 * mm});
            skCircle(sketch, "E168", {"center": v(185.4, 0) * mm, "radius": 3.4 * mm});
            skCircle(sketch, "E169", {"center": v(210.4, -25) * mm, "radius": 3.4 * mm});
            skCircle(sketch, "E170", {"center": v(350.4, -125) * mm, "radius": 3.4 * mm});
            skCircle(sketch, "E171", {"center": v(375.4, -150) * mm, "radius": 3.4 * mm});
            skCircle(sketch, "E172", {"center": v(400.4, -175) * mm, "radius": 3.4 * mm});
            skLineSegment(sketch, "E173", {"start": v(280.4, -200) * mm, "end": v(280.4, 50) * mm});
            skLineSegment(sketch, "E174", {"start": v(130.4, -75) * mm, "end": v(430.4, -75) * mm});
            skLineSegment(sketch, "E175", {"start": v(312.78, -165) * mm, "end": v(312.78, -200) * mm});
            skLineSegment(sketch, "E176", {"start": v(334.68, 50) * mm, "end": v(334.68, 15) * mm});
            skSolve(sketch);
        }
        {
            var Q0;
            Q0 = qSketchRegion(id + "F15", true);
            extrude(context, id + "F16", {"entities" : qUnion([Q0]), "oppositeDirection" : true, "depth" : 25 * mm, "offsetDistance" : 25 * mm});
        }
        {
            var Q0;
            Q0=sQuery(id+"F15.wireOp",VERTEX,"E167.center");
            var Q1;
            Q1=sQuery(id+"F15.wireOp",VERTEX,"E166.center");
            var Q2;
            Q2=sQuery(id+"F15.wireOp",VERTEX,"E165.center");
            var Q3;
            Q3=sQuery(id+"F15.wireOp",VERTEX,"E161.center");
            var Q4;
            Q4=sQuery(id+"F15.wireOp",VERTEX,"E162.center");
            var Q5;
            Q5=sQuery(id+"F15.wireOp",VERTEX,"E163.center");
            var Q6;
            Q6=makeQuery(id+"F16.opExtrude","SWEPT_BODY",BODY,{"disambiguationData":[OSD([sQuery(id+"F15.wireOp",EDGE,"E144.bottom"),sQuery(id+"F15.wireOp",EDGE,"E144.top"),sQuery(id+"F15.wireOp",EDGE,"E144.left"),sQuery(id+"F15.wireOp",EDGE,"E144.right"),sQuery(id+"F15.wireOp",EDGE,"E145"),sQuery(id+"F15.wireOp",EDGE,"E146"),sQuery(id+"F15.wireOp",EDGE,"E147"),sQuery(id+"F15.wireOp",EDGE,"E148"),sQuery(id+"F15.wireOp",EDGE,"E149"),sQuery(id+"F15.wireOp",EDGE,"E150"),sQuery(id+"F15.wireOp",EDGE,"E151"),sQuery(id+"F15.wireOp",EDGE,"E152"),sQuery(id+"F15.wireOp",EDGE,"E153"),sQuery(id+"F15.wireOp",EDGE,"E154"),sQuery(id+"F15.wireOp",EDGE,"E155"),sQuery(id+"F15.wireOp",EDGE,"E156"),sQuery(id+"F15.wireOp",EDGE,"E157"),sQuery(id+"F15.wireOp",EDGE,"E158"),sQuery(id+"F15.wireOp",EDGE,"E159"),sQuery(id+"F15.wireOp",EDGE,"E160"),sQuery(id+"F15.wireOp",EDGE,"E161"),sQuery(id+"F15.wireOp",EDGE,"E162"),sQuery(id+"F15.wireOp",EDGE,"E163"),sQuery(id+"F15.wireOp",EDGE,"E164"),sQuery(id+"F15.wireOp",EDGE,"E165"),sQuery(id+"F15.wireOp",EDGE,"E166"),sQuery(id+"F15.wireOp",EDGE,"E167"),sQuery(id+"F15.wireOp",EDGE,"E168"),sQuery(id+"F15.wireOp",EDGE,"E169"),sQuery(id+"F15.wireOp",EDGE,"E170"),sQuery(id+"F15.wireOp",EDGE,"E171"),sQuery(id+"F15.wireOp",EDGE,"E172")])]});
            hole(context, id + "F17", {"style" : HoleStyle.C_BORE, "endStyle" : HoleEndStyle.BLIND, "holeDiameter" : 5 * mm, "cBoreDiameter" : 15 * mm, "cBoreDepth" : 1 * mm, "majorDiameter" : 5 * mm, "holeDepth" : 50 * mm, "isTappedThrough" : true, "tappedDepth" : 12 * mm, "tapClearance" : 3, "locations" : qUnion([Q0, Q1, Q2, Q3, Q4, Q5]), "scope" : qUnion([Q6]), "startStyle" : HoleStartStyle.SKETCH});
        }
        {
            var Q0;
            Q0=sQuery(id+"F15.wireOp",VERTEX,"E161.center");
            var Q1;
            Q1=sQuery(id+"F15.wireOp",VERTEX,"E167.center");
            var Q2;
            Q2=makeQuery(id+"F1.opExtrude","SWEPT_BODY",BODY,{"disambiguationData":[OSD([sQuery(id+"F0.wireOp",EDGE,"E0.bottom"),sQuery(id+"F0.wireOp",EDGE,"E0.top"),sQuery(id+"F0.wireOp",EDGE,"E0.left"),sQuery(id+"F0.wireOp",EDGE,"E3"),sQuery(id+"F0.wireOp",EDGE,"E4"),sQuery(id+"F0.wireOp",EDGE,"E6"),sQuery(id+"F0.wireOp",EDGE,"E7"),sQuery(id+"F0.wireOp",EDGE,"E8"),sQuery(id+"F0.wireOp",EDGE,"E12"),sQuery(id+"F0.wireOp",EDGE,"E13"),sQuery(id+"F0.wireOp",EDGE,"E14"),sQuery(id+"F0.wireOp",EDGE,"E15"),sQuery(id+"F0.wireOp",EDGE,"E16"),sQuery(id+"F0.wireOp",EDGE,"E18"),sQuery(id+"F0.wireOp",EDGE,"E19"),sQuery(id+"F0.wireOp",EDGE,"E22"),sQuery(id+"F0.wireOp",EDGE,"E23"),sQuery(id+"F0.wireOp",EDGE,"E24"),sQuery(id+"F0.wireOp",EDGE,"E27"),sQuery(id+"F0.wireOp",EDGE,"E28"),sQuery(id+"F0.wireOp",EDGE,"E29"),sQuery(id+"F0.wireOp",EDGE,"E31"),sQuery(id+"F0.wireOp",EDGE,"E32"),sQuery(id+"F0.wireOp",EDGE,"E34"),sQuery(id+"F0.wireOp",EDGE,"E35"),sQuery(id+"F0.wireOp",EDGE,"E36.bottom"),sQuery(id+"F0.wireOp",EDGE,"E36.top"),sQuery(id+"F0.wireOp",EDGE,"E36.right"),sQuery(id+"F0.wireOp",EDGE,"E39"),sQuery(id+"F0.wireOp",EDGE,"E40"),sQuery(id+"F0.wireOp",EDGE,"E42"),sQuery(id+"F0.wireOp",EDGE,"E43"),sQuery(id+"F0.wireOp",EDGE,"E44"),sQuery(id+"F0.wireOp",EDGE,"E48"),sQuery(id+"F0.wireOp",EDGE,"E49"),sQuery(id+"F0.wireOp",EDGE,"E50"),sQuery(id+"F0.wireOp",EDGE,"E51"),sQuery(id+"F0.wireOp",EDGE,"E52"),sQuery(id+"F0.wireOp",EDGE,"E54"),sQuery(id+"F0.wireOp",EDGE,"E55"),sQuery(id+"F0.wireOp",EDGE,"E58"),sQuery(id+"F0.wireOp",EDGE,"E59"),sQuery(id+"F0.wireOp",EDGE,"E60"),sQuery(id+"F0.wireOp",EDGE,"E63"),sQuery(id+"F0.wireOp",EDGE,"E64"),sQuery(id+"F0.wireOp",EDGE,"E65"),sQuery(id+"F0.wireOp",EDGE,"E67"),sQuery(id+"F0.wireOp",EDGE,"E68"),sQuery(id+"F0.wireOp",EDGE,"E70"),sQuery(id+"F0.wireOp",EDGE,"E71"),sQuery(id+"F0.wireOp",EDGE,"E72"),sQuery(id+"F0.wireOp",EDGE,"E73"),sQuery(id+"F0.wireOp",EDGE,"E74"),sQuery(id+"F0.wireOp",EDGE,"E75"),sQuery(id+"F0.wireOp",EDGE,"E76"),sQuery(id+"F0.wireOp",EDGE,"E80"),sQuery(id+"F0.wireOp",EDGE,"E81"),sQuery(id+"F0.wireOp",EDGE,"E82"),sQuery(id+"F0.wireOp",EDGE,"E83"),sQuery(id+"F0.wireOp",EDGE,"E84"),sQuery(id+"F0.wireOp",EDGE,"E88"),sQuery(id+"F0.wireOp",EDGE,"E89"),sQuery(id+"F0.wireOp",EDGE,"E90")])]});
            hole(context, id + "F18", {"style" : HoleStyle.SIMPLE, "endStyle" : HoleEndStyle.BLIND, "oppositeDirection" : true, "holeDiameter" : 10 * mm, "majorDiameter" : 5 * mm, "holeDepth" : 50 * mm, "isTappedThrough" : true, "tappedDepth" : 12 * mm, "tapClearance" : 3, "locations" : qUnion([Q0, Q1]), "scope" : qUnion([Q2]), "startStyle" : HoleStartStyle.SKETCH});
        }
        {
            var Q0;
            Q0=sQuery(id+"F15.wireOp",VERTEX,"E170.center");
            var Q1;
            Q1=makeQuery(id+"F1.opExtrude","SWEPT_BODY",BODY,{"disambiguationData":[OSD([sQuery(id+"F0.wireOp",EDGE,"E0.bottom"),sQuery(id+"F0.wireOp",EDGE,"E0.top"),sQuery(id+"F0.wireOp",EDGE,"E0.left"),sQuery(id+"F0.wireOp",EDGE,"E3"),sQuery(id+"F0.wireOp",EDGE,"E4"),sQuery(id+"F0.wireOp",EDGE,"E6"),sQuery(id+"F0.wireOp",EDGE,"E7"),sQuery(id+"F0.wireOp",EDGE,"E8"),sQuery(id+"F0.wireOp",EDGE,"E12"),sQuery(id+"F0.wireOp",EDGE,"E13"),sQuery(id+"F0.wireOp",EDGE,"E14"),sQuery(id+"F0.wireOp",EDGE,"E15"),sQuery(id+"F0.wireOp",EDGE,"E16"),sQuery(id+"F0.wireOp",EDGE,"E18"),sQuery(id+"F0.wireOp",EDGE,"E19"),sQuery(id+"F0.wireOp",EDGE,"E22"),sQuery(id+"F0.wireOp",EDGE,"E23"),sQuery(id+"F0.wireOp",EDGE,"E24"),sQuery(id+"F0.wireOp",EDGE,"E27"),sQuery(id+"F0.wireOp",EDGE,"E28"),sQuery(id+"F0.wireOp",EDGE,"E29"),sQuery(id+"F0.wireOp",EDGE,"E31"),sQuery(id+"F0.wireOp",EDGE,"E32"),sQuery(id+"F0.wireOp",EDGE,"E34"),sQuery(id+"F0.wireOp",EDGE,"E35"),sQuery(id+"F0.wireOp",EDGE,"E36.bottom"),sQuery(id+"F0.wireOp",EDGE,"E36.top"),sQuery(id+"F0.wireOp",EDGE,"E36.right"),sQuery(id+"F0.wireOp",EDGE,"E39"),sQuery(id+"F0.wireOp",EDGE,"E40"),sQuery(id+"F0.wireOp",EDGE,"E42"),sQuery(id+"F0.wireOp",EDGE,"E43"),sQuery(id+"F0.wireOp",EDGE,"E44"),sQuery(id+"F0.wireOp",EDGE,"E48"),sQuery(id+"F0.wireOp",EDGE,"E49"),sQuery(id+"F0.wireOp",EDGE,"E50"),sQuery(id+"F0.wireOp",EDGE,"E51"),sQuery(id+"F0.wireOp",EDGE,"E52"),sQuery(id+"F0.wireOp",EDGE,"E54"),sQuery(id+"F0.wireOp",EDGE,"E55"),sQuery(id+"F0.wireOp",EDGE,"E58"),sQuery(id+"F0.wireOp",EDGE,"E59"),sQuery(id+"F0.wireOp",EDGE,"E60"),sQuery(id+"F0.wireOp",EDGE,"E63"),sQuery(id+"F0.wireOp",EDGE,"E64"),sQuery(id+"F0.wireOp",EDGE,"E65"),sQuery(id+"F0.wireOp",EDGE,"E67"),sQuery(id+"F0.wireOp",EDGE,"E68"),sQuery(id+"F0.wireOp",EDGE,"E70"),sQuery(id+"F0.wireOp",EDGE,"E71"),sQuery(id+"F0.wireOp",EDGE,"E72"),sQuery(id+"F0.wireOp",EDGE,"E73"),sQuery(id+"F0.wireOp",EDGE,"E74"),sQuery(id+"F0.wireOp",EDGE,"E75"),sQuery(id+"F0.wireOp",EDGE,"E76"),sQuery(id+"F0.wireOp",EDGE,"E80"),sQuery(id+"F0.wireOp",EDGE,"E81"),sQuery(id+"F0.wireOp",EDGE,"E82"),sQuery(id+"F0.wireOp",EDGE,"E83"),sQuery(id+"F0.wireOp",EDGE,"E84"),sQuery(id+"F0.wireOp",EDGE,"E88"),sQuery(id+"F0.wireOp",EDGE,"E89"),sQuery(id+"F0.wireOp",EDGE,"E90")])]});
            hole(context, id + "F19", {"style" : HoleStyle.SIMPLE, "endStyle" : HoleEndStyle.BLIND, "oppositeDirection" : true, "standardTappedOrClearance" : lookupTablePath({ "fit" : "Normal", "standard" : "ISO", "size" : "M8", "type" : "Clearance" }), "standardBlindInLast" : lookupTablePath({ "fit" : "Normal", "standard" : "ISO", "size" : "M8", "type" : "Clearance" }), "holeDiameter" : 9 * mm, "majorDiameter" : 5 * mm, "holeDepth" : 50 * mm, "isTappedThrough" : true, "tappedDepth" : 12 * mm, "tapClearance" : 3, "locations" : qUnion([Q0]), "scope" : qUnion([Q1]), "startStyle" : HoleStartStyle.SKETCH});
        }
        {
            var Q0;
            Q0=makeQuery(id+"F1.opExtrude","CAP_FACE",FACE,{"disambiguationData":[OSD([sQuery(id+"F0.wireOp",EDGE,"E0.bottom"),sQuery(id+"F0.wireOp",EDGE,"E0.top"),sQuery(id+"F0.wireOp",EDGE,"E0.left"),sQuery(id+"F0.wireOp",EDGE,"E3"),sQuery(id+"F0.wireOp",EDGE,"E4"),sQuery(id+"F0.wireOp",EDGE,"E6"),sQuery(id+"F0.wireOp",EDGE,"E7"),sQuery(id+"F0.wireOp",EDGE,"E8"),sQuery(id+"F0.wireOp",EDGE,"E12"),sQuery(id+"F0.wireOp",EDGE,"E13"),sQuery(id+"F0.wireOp",EDGE,"E14"),sQuery(id+"F0.wireOp",EDGE,"E15"),sQuery(id+"F0.wireOp",EDGE,"E16"),sQuery(id+"F0.wireOp",EDGE,"E18"),sQuery(id+"F0.wireOp",EDGE,"E19"),sQuery(id+"F0.wireOp",EDGE,"E22"),sQuery(id+"F0.wireOp",EDGE,"E23"),sQuery(id+"F0.wireOp",EDGE,"E24"),sQuery(id+"F0.wireOp",EDGE,"E27"),sQuery(id+"F0.wireOp",EDGE,"E28"),sQuery(id+"F0.wireOp",EDGE,"E29"),sQuery(id+"F0.wireOp",EDGE,"E31"),sQuery(id+"F0.wireOp",EDGE,"E32"),sQuery(id+"F0.wireOp",EDGE,"E34"),sQuery(id+"F0.wireOp",EDGE,"E35"),sQuery(id+"F0.wireOp",EDGE,"E36.bottom"),sQuery(id+"F0.wireOp",EDGE,"E36.top"),sQuery(id+"F0.wireOp",EDGE,"E36.right"),sQuery(id+"F0.wireOp",EDGE,"E39"),sQuery(id+"F0.wireOp",EDGE,"E40"),sQuery(id+"F0.wireOp",EDGE,"E42"),sQuery(id+"F0.wireOp",EDGE,"E43"),sQuery(id+"F0.wireOp",EDGE,"E44"),sQuery(id+"F0.wireOp",EDGE,"E48"),sQuery(id+"F0.wireOp",EDGE,"E49"),sQuery(id+"F0.wireOp",EDGE,"E50"),sQuery(id+"F0.wireOp",EDGE,"E51"),sQuery(id+"F0.wireOp",EDGE,"E52"),sQuery(id+"F0.wireOp",EDGE,"E54"),sQuery(id+"F0.wireOp",EDGE,"E55"),sQuery(id+"F0.wireOp",EDGE,"E58"),sQuery(id+"F0.wireOp",EDGE,"E59"),sQuery(id+"F0.wireOp",EDGE,"E60"),sQuery(id+"F0.wireOp",EDGE,"E63"),sQuery(id+"F0.wireOp",EDGE,"E64"),sQuery(id+"F0.wireOp",EDGE,"E65"),sQuery(id+"F0.wireOp",EDGE,"E67"),sQuery(id+"F0.wireOp",EDGE,"E68"),sQuery(id+"F0.wireOp",EDGE,"E70"),sQuery(id+"F0.wireOp",EDGE,"E71"),sQuery(id+"F0.wireOp",EDGE,"E72"),sQuery(id+"F0.wireOp",EDGE,"E73"),sQuery(id+"F0.wireOp",EDGE,"E74"),sQuery(id+"F0.wireOp",EDGE,"E75"),sQuery(id+"F0.wireOp",EDGE,"E76"),sQuery(id+"F0.wireOp",EDGE,"E80"),sQuery(id+"F0.wireOp",EDGE,"E81"),sQuery(id+"F0.wireOp",EDGE,"E82"),sQuery(id+"F0.wireOp",EDGE,"E83"),sQuery(id+"F0.wireOp",EDGE,"E84"),sQuery(id+"F0.wireOp",EDGE,"E88"),sQuery(id+"F0.wireOp",EDGE,"E89"),sQuery(id+"F0.wireOp",EDGE,"E90")])],"isStart":false});
            var sketch = newSketch(context, id + "F20", { "sketchPlane" : qUnion([Q0])});
            skLineSegment(sketch, "E177", {"start": v(203.5, 0) * mm, "end": v(203.5, -101.5) * mm});
            skLineSegment(sketch, "E178", {"start": v(203.5, -101.5) * mm, "end": v(203.5, -101.5) * mm});
            skLineSegment(sketch, "E179", {"start": v(203.5, -101.5) * mm, "end": v(203.5, -180) * mm});
            skLineSegment(sketch, "E180", {"start": v(203.5, 0) * mm, "end": v(200.5, 0) * mm});
            skLineSegment(sketch, "E181", {"start": v(200.5, 0) * mm, "end": v(200.5, -98.5) * mm});
            skLineSegment(sketch, "E182", {"start": v(200.5, -98.5) * mm, "end": v(200.5, -98.5) * mm});
            skLineSegment(sketch, "E183", {"start": v(200.5, -98.5) * mm, "end": v(200.5, -180) * mm});
            skLineSegment(sketch, "E184", {"start": v(200.5, -180) * mm, "end": v(203.5, -180) * mm});
            skLineSegment(sketch, "E185", {"start": v(203.5, -101.5) * mm, "end": v(203.5, -98.5) * mm});
            skLineSegment(sketch, "E186", {"start": v(200.5, -98.5) * mm, "end": v(203.5, -98.5) * mm});
            skPoint(sketch, "E187", {"position": v(202, 0) * mm});
            skPoint(sketch, "E188", {"position": v(202, -180) * mm});
            skPoint(sketch, "E189", {"position": v(203.5, -100) * mm});
            skSolve(sketch);
        }
        {
            var Q0;
            Q0 = qSketchRegion(id + "F20", true);
            extrude(context, id + "F21", {"entities" : qUnion([Q0]), "operationType" : NewBodyOperationType.REMOVE, "oppositeDirection" : true, "depth" : 5 * mm, "offsetDistance" : 25 * mm});
        }
    });
